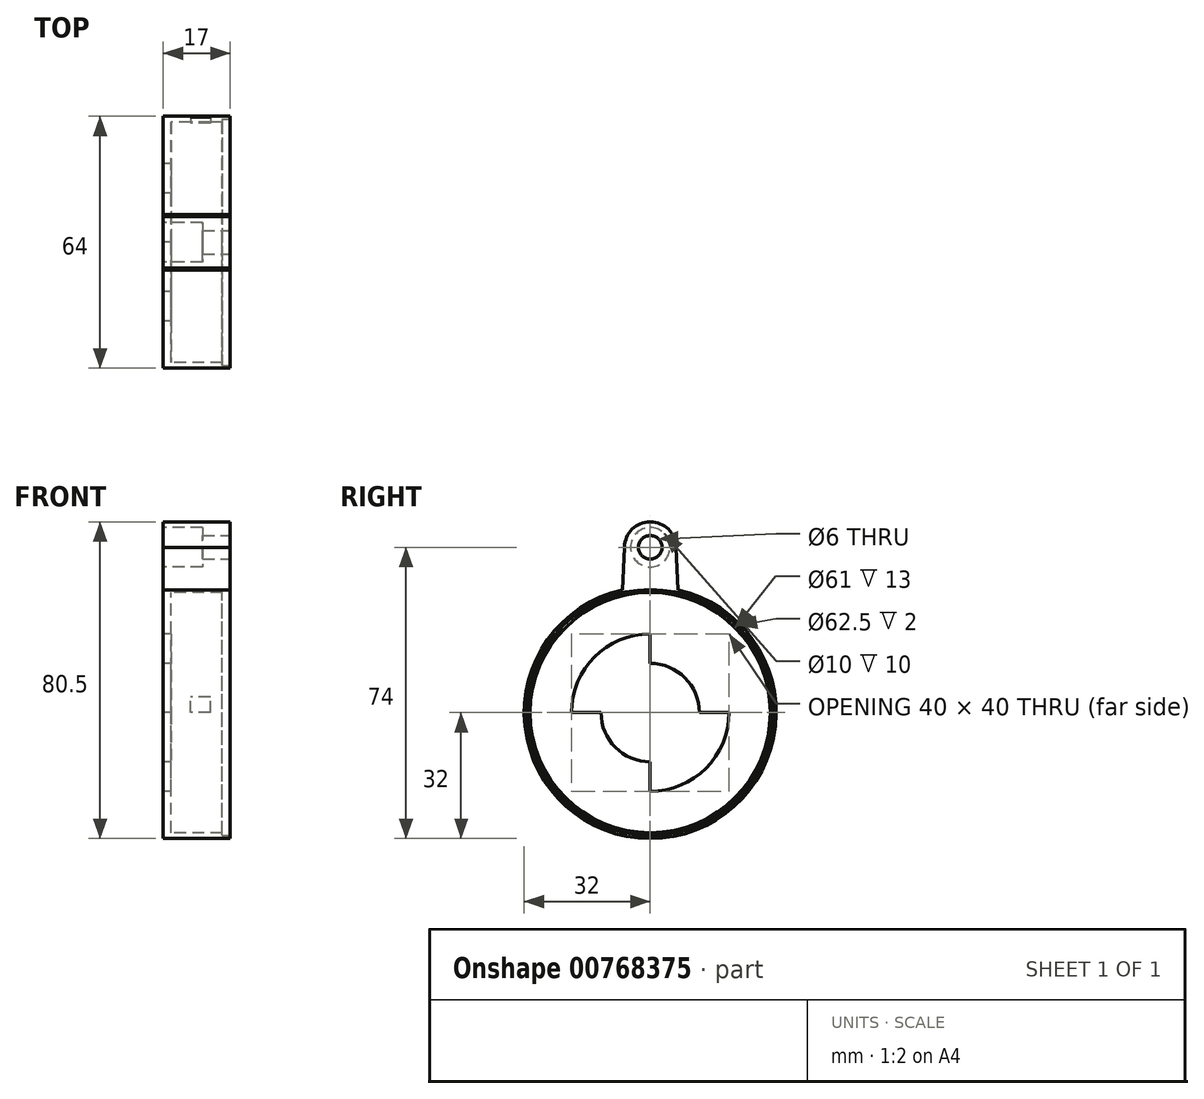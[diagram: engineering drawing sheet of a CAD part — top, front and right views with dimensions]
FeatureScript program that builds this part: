
annotation { "Feature Type Name" : "Feature", "Feature Type Description" : "" }
export const myFeature = defineFeature(function(context is Context, id is Id, definition is map)
    precondition{}
    {
        {
            var Q0;
            Q0=qCreatedBy(makeId("Right.planeOp"),FACE);
            var sketch = newSketch(context, id + "F0", { "sketchPlane" : qUnion([Q0])});
            skCircle(sketch, "E0", {"center": v(0, 0) * mm, "radius": 9.5 * mm});
            skCircle(sketch, "E1", {"center": v(0, 0) * mm, "radius": 30.5 * mm});
            skSolve(sketch);
        }
        {
            var Q0;
            Q0=makeQuery(id+"F0.imprint","IMPRINT",FACE,{"disambiguationData":[TD([[makeQuery(id+"F0.imprint","IMPRINT",EDGE,{"derivedFrom":sQuery(id+"F0.wireOp",EDGE,"E0")}),-1.0]])]});
            extrude(context, id + "F1", {"entities" : qUnion([Q0]), "depth" : 2 * mm, "offsetDistance" : 25 * mm});
        }
        {
            var Q0;
            Q0=makeQuery(id+"F1.opExtrude","CAP_FACE",FACE,{"disambiguationData":[OSD([sQuery(id+"F0.wireOp",EDGE,"E0"),sQuery(id+"F0.wireOp",EDGE,"E1")])],"isStart":true});
            var sketch = newSketch(context, id + "F2", { "sketchPlane" : qUnion([Q0])});
            skCircle(sketch, "E2", {"center": v(0, 0) * mm, "radius": 32 * mm});
            skSolve(sketch);
        }
        {
            var Q0;
            Q0=makeQuery(id+"F2.imprint","IMPRINT",FACE,{"disambiguationData":[TD([[makeQuery(id+"F2.imprint","IMPRINT",EDGE,{"derivedFrom":sQuery(id+"F2.wireOp",EDGE,"E2")}),1.0]])]});
            extrude(context, id + "F3", {"entities" : qUnion([Q0]), "operationType" : NewBodyOperationType.ADD, "oppositeDirection" : true, "depth" : 17 * mm, "offsetDistance" : 25 * mm});
        }
        {
            var Q0;
            Q0=makeQuery(id+"F3.opExtrude","CAP_FACE",FACE,{"disambiguationData":[OSD([sQuery(id+"F0.wireOp",EDGE,"E1"),sQuery(id+"F2.wireOp",EDGE,"E2")])],"isStart":false});
            var sketch = newSketch(context, id + "F4", { "sketchPlane" : qUnion([Q0])});
            skCircle(sketch, "E3", {"center": v(0, 42) * mm, "radius": 6.5 * mm});
            skLineSegment(sketch, "E4", {"start": v(10.44, 42) * mm, "end": v(-12.18, 42) * mm, "construction": true});
            skLineSegment(sketch, "E5", {"start": v(-7, 31.22) * mm, "end": v(-6.5, 42) * mm});
            skLineSegment(sketch, "E6", {"start": v(7, 31.22) * mm, "end": v(6.5, 42) * mm});
            skCircle(sketch, "E7", {"center": v(0, 42) * mm, "radius": 3 * mm});
            skSolve(sketch);
        }
        {
            var Q0;
            Q0=makeQuery(id+"F4.imprint","IMPRINT",FACE,{"disambiguationData":[TD([[makeQuery(id+"F4.imprint","IMPRINT",EDGE,{"derivedFrom":sQuery(id+"F4.wireOp",EDGE,"E7")}),-1.0]])]});
            var Q1;
            {var subQ0=sQuery(id+"F4.wireOp",EDGE,"E5");Q1=makeQuery(id+"F4.imprint","IMPRINT",FACE,{"disambiguationData":[TD([[makeQuery(id+"F4.imprint","IMPRINT",EDGE,{"derivedFrom":subQ0}),-1.0]])]});}
            extrude(context, id + "F5", {"entities" : qUnion([Q0, Q1]), "operationType" : NewBodyOperationType.ADD, "oppositeDirection" : true, "depth" : 17 * mm, "offsetDistance" : 25 * mm});
        }
        {
            var Q0;
            {var subQ0=sQuery(id+"F4.wireOp",EDGE,"E7");var subQ1=sQuery(id+"F4.wireOp",EDGE,"E6");var subQ2=sQuery(id+"F4.wireOp",EDGE,"E5");var subQ3=sQuery(id+"F4.wireOp",EDGE,"E3");var subQ4=sQuery(id+"F2.wireOp",EDGE,"E2");Q0=makeQuery(id+"F6pJBYTK8aANDv5_1.2.F5.boolean.opBoolean","MERGE",FACE,{"derivedFrom":[makeQuery(id+"F6pJBYTK8aANDv5_1.1.F5.boolean.opBoolean","MERGE",FACE,{"derivedFrom":[makeQuery(id+"F5.boolean.opBoolean","MERGE",FACE,{"derivedFrom":[makeQuery(id+"F3.opExtrude","CAP_FACE",FACE,{"disambiguationData":[OSD([sQuery(id+"F0.wireOp",EDGE,"E1"),subQ4])],"isStart":false}),makeQuery(id+"F5.opExtrude","CAP_FACE",FACE,{"disambiguationData":[OSD([subQ4,subQ3,subQ2,subQ1,subQ0])],"isStart":true})]}),makeQuery(id+"F6pJBYTK8aANDv5_1.1.F5.opExtrude","CAP_FACE",FACE,{"disambiguationData":[OSD([subQ4,subQ3,subQ2,subQ1,subQ0])],"isStart":true})]}),makeQuery(id+"F6pJBYTK8aANDv5_1.2.F5.opExtrude","CAP_FACE",FACE,{"disambiguationData":[OSD([subQ4,subQ3,subQ2,subQ1,subQ0])],"isStart":true})]});}
            var sketch = newSketch(context, id + "F6", { "sketchPlane" : qUnion([Q0])});
            skCircle(sketch, "E8", {"center": v(0, 0) * mm, "radius": 31.25 * mm});
            skSolve(sketch);
        }
        {
            var Q0;
            Q0=makeQuery(id+"F6.imprint","IMPRINT",FACE,{"disambiguationData":[TD([[makeQuery(id+"F6.imprint","IMPRINT",EDGE,{"derivedFrom":sQuery(id+"F6.wireOp",EDGE,"E8")}),1.0]])]});
            extrude(context, id + "F7", {"entities" : qUnion([Q0]), "operationType" : NewBodyOperationType.REMOVE, "oppositeDirection" : true, "depth" : 2 * mm, "offsetDistance" : 25 * mm});
        }
        {
            var Q0;
            Q0=qCreatedBy(makeId("Front.planeOp"),FACE);
            var sketch = newSketch(context, id + "F8", { "sketchPlane" : qUnion([Q0])});
            skLineSegment(sketch, "E9.bottom", {"start": v(7, 0) * mm, "end": v(12, 0) * mm});
            skLineSegment(sketch, "E9.top", {"start": v(7, 4) * mm, "end": v(12, 4) * mm});
            skLineSegment(sketch, "E9.left", {"start": v(7, 0) * mm, "end": v(7, 4) * mm});
            skLineSegment(sketch, "E9.right", {"start": v(12, 0) * mm, "end": v(12, 4) * mm});
            skSolve(sketch);
        }
        {
            var Q0;
            Q0=makeQuery(id+"F8.imprint","IMPRINT",FACE,{"disambiguationData":[TD([[makeQuery(id+"F8.imprint","IMPRINT",EDGE,{"derivedFrom":sQuery(id+"F8.wireOp",EDGE,"E9.bottom")}),1.0]])]});
            extrude(context, id + "F9", {"entities" : qUnion([Q0]), "operationType" : NewBodyOperationType.REMOVE, "oppositeDirection" : true, "depth" : 43.1 * mm, "offsetDistance" : 25 * mm});
        }
        {
            var Q0;
            {var subQ0=sQuery(id+"F4.wireOp",EDGE,"E7");var subQ1=sQuery(id+"F4.wireOp",EDGE,"E6");var subQ2=sQuery(id+"F4.wireOp",EDGE,"E5");var subQ3=sQuery(id+"F4.wireOp",EDGE,"E3");var subQ4=sQuery(id+"F2.wireOp",EDGE,"E2");var subQ5=sQuery(id+"F0.wireOp",EDGE,"E1");Q0=makeQuery(id+"F6pJBYTK8aANDv5_1.2.F5.boolean.opBoolean","MERGE",FACE,{"derivedFrom":[makeQuery(id+"F6pJBYTK8aANDv5_1.1.F5.boolean.opBoolean","MERGE",FACE,{"derivedFrom":[makeQuery(id+"F5.boolean.opBoolean","MERGE",FACE,{"derivedFrom":[makeQuery(id+"F3.boolean.opBoolean","MERGE",FACE,{"derivedFrom":[makeQuery(id+"F1.opExtrude","CAP_FACE",FACE,{"disambiguationData":[OSD([sQuery(id+"F0.wireOp",EDGE,"E0"),subQ5])],"isStart":true}),makeQuery(id+"F3.opExtrude","CAP_FACE",FACE,{"disambiguationData":[OSD([subQ5,subQ4])],"isStart":true})]}),makeQuery(id+"F5.opExtrude","CAP_FACE",FACE,{"disambiguationData":[OSD([subQ4,subQ3,subQ2,subQ1,subQ0])],"isStart":false})]}),makeQuery(id+"F6pJBYTK8aANDv5_1.1.F5.opExtrude","CAP_FACE",FACE,{"disambiguationData":[OSD([subQ4,subQ3,subQ2,subQ1,subQ0])],"isStart":false})]}),makeQuery(id+"F6pJBYTK8aANDv5_1.2.F5.opExtrude","CAP_FACE",FACE,{"disambiguationData":[OSD([subQ4,subQ3,subQ2,subQ1,subQ0])],"isStart":false})]});}
            var sketch = newSketch(context, id + "F10", { "sketchPlane" : qUnion([Q0])});
            skCircle(sketch, "E10", {"center": v(0, 42) * mm, "radius": 5 * mm});
            skCircle(sketch, "E11", {"center": v(36.37, -21) * mm, "radius": 5 * mm});
            skCircle(sketch, "E12", {"center": v(-36.37, -21) * mm, "radius": 5 * mm});
            skSolve(sketch);
        }
        {
            var Q0;
            Q0=makeQuery(id+"F10.imprint","IMPRINT",FACE,{"disambiguationData":[TD([[makeQuery(id+"F10.imprint","IMPRINT",EDGE,{"derivedFrom":sQuery(id+"F10.wireOp",EDGE,"E12")}),1.0]])]});
            var Q1;
            Q1=makeQuery(id+"F10.imprint","IMPRINT",FACE,{"disambiguationData":[TD([[makeQuery(id+"F10.imprint","IMPRINT",EDGE,{"derivedFrom":sQuery(id+"F10.wireOp",EDGE,"E10")}),1.0]])]});
            var Q2;
            Q2=makeQuery(id+"F10.imprint","IMPRINT",FACE,{"disambiguationData":[TD([[makeQuery(id+"F10.imprint","IMPRINT",EDGE,{"derivedFrom":sQuery(id+"F10.wireOp",EDGE,"E11")}),1.0]])]});
            extrude(context, id + "F11", {"entities" : qUnion([Q0, Q1, Q2]), "operationType" : NewBodyOperationType.REMOVE, "oppositeDirection" : true, "depth" : 10 * mm, "offsetDistance" : 25 * mm});
        }
        {
            var Q0;
            {var subQ0=sQuery(id+"F4.wireOp",EDGE,"E7");var subQ1=sQuery(id+"F4.wireOp",EDGE,"E6");var subQ2=sQuery(id+"F4.wireOp",EDGE,"E5");var subQ3=sQuery(id+"F4.wireOp",EDGE,"E3");var subQ4=sQuery(id+"F2.wireOp",EDGE,"E2");var subQ5=sQuery(id+"F0.wireOp",EDGE,"E1");Q0=makeQuery(id+"F6pJBYTK8aANDv5_1.2.F5.boolean.opBoolean","MERGE",FACE,{"derivedFrom":[makeQuery(id+"F6pJBYTK8aANDv5_1.1.F5.boolean.opBoolean","MERGE",FACE,{"derivedFrom":[makeQuery(id+"F5.boolean.opBoolean","MERGE",FACE,{"derivedFrom":[makeQuery(id+"F3.boolean.opBoolean","MERGE",FACE,{"derivedFrom":[makeQuery(id+"F1.opExtrude","CAP_FACE",FACE,{"disambiguationData":[OSD([sQuery(id+"F0.wireOp",EDGE,"E0"),subQ5])],"isStart":true}),makeQuery(id+"F3.opExtrude","CAP_FACE",FACE,{"disambiguationData":[OSD([subQ5,subQ4])],"isStart":true})]}),makeQuery(id+"F5.opExtrude","CAP_FACE",FACE,{"disambiguationData":[OSD([subQ4,subQ3,subQ2,subQ1,subQ0])],"isStart":false})]}),makeQuery(id+"F6pJBYTK8aANDv5_1.1.F5.opExtrude","CAP_FACE",FACE,{"disambiguationData":[OSD([subQ4,subQ3,subQ2,subQ1,subQ0])],"isStart":false})]}),makeQuery(id+"F6pJBYTK8aANDv5_1.2.F5.opExtrude","CAP_FACE",FACE,{"disambiguationData":[OSD([subQ4,subQ3,subQ2,subQ1,subQ0])],"isStart":false})]});}
            var sketch = newSketch(context, id + "F12", { "sketchPlane" : qUnion([Q0])});
            skArc(sketch, "E13", {"start": v(-20, 0) * mm, "mid": v(-14.14, -14.14) * mm, "end": v(0, -20) * mm});
            skLineSegment(sketch, "E14", {"start": v(-12.5, 0) * mm, "end": v(-20, 0) * mm});
            skLineSegment(sketch, "E15", {"start": v(0, -12.5) * mm, "end": v(0, -20) * mm});
            skLineSegment(sketch, "E16", {"start": v(0, 12.5) * mm, "end": v(0, 20) * mm});
            skLineSegment(sketch, "E17", {"start": v(12.5, 0) * mm, "end": v(20, 0) * mm});
            skArc(sketch, "E18", {"start": v(0, 12.5) * mm, "mid": v(-8.84, 8.84) * mm, "end": v(-12.5, 0) * mm});
            skArc(sketch, "E19.trimOffspring", {"start": v(0, -12.5) * mm, "mid": v(8.84, -8.84) * mm, "end": v(12.5, 0) * mm});
            skArc(sketch, "E20.trimOffspring", {"start": v(20, 0) * mm, "mid": v(14.14, 14.14) * mm, "end": v(0, 20) * mm});
            skSolve(sketch);
        }
        {
            var Q0;
            Q0=makeQuery(id+"F12.imprint","IMPRINT",FACE,{"disambiguationData":[TD([[makeQuery(id+"F12.imprint","IMPRINT",EDGE,{"derivedFrom":sQuery(id+"F12.wireOp",EDGE,"E13")}),1.0]])]});
            extrude(context, id + "F13", {"entities" : qUnion([Q0]), "operationType" : NewBodyOperationType.REMOVE, "oppositeDirection" : true, "depth" : 25 * mm, "offsetDistance" : 25 * mm});
        }
    });
